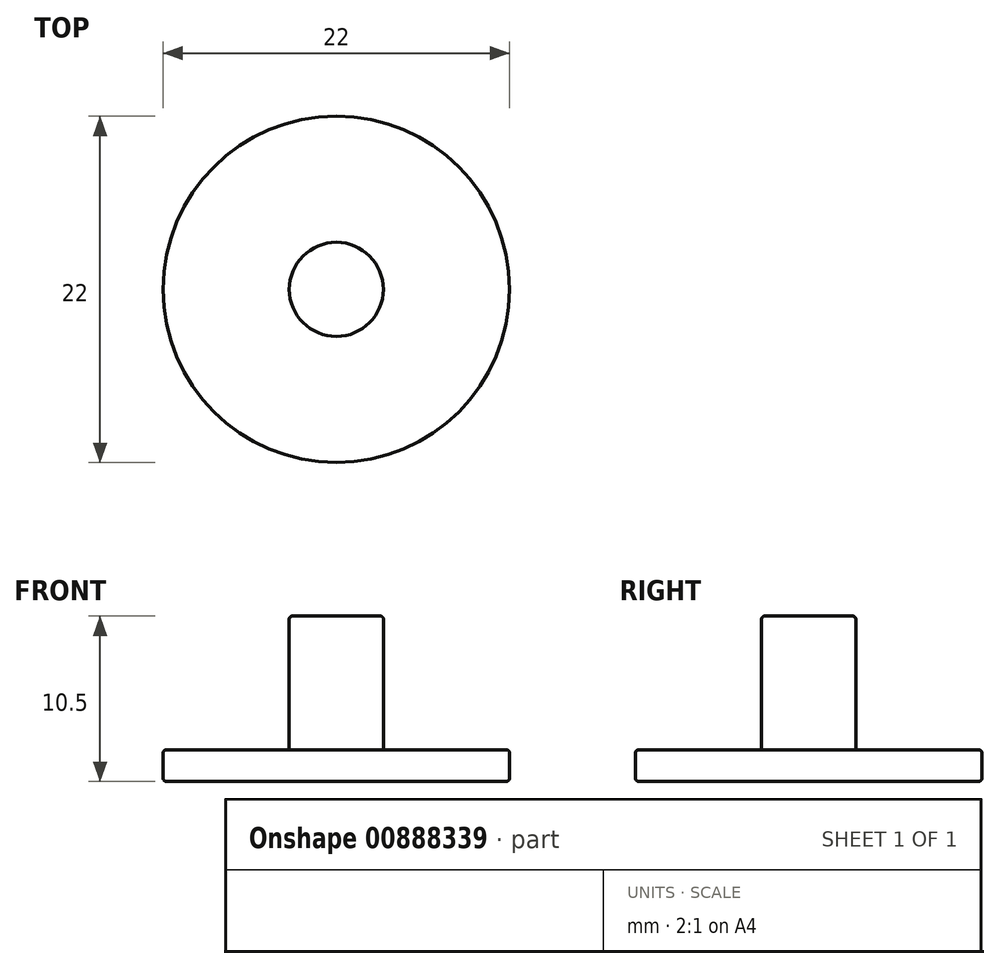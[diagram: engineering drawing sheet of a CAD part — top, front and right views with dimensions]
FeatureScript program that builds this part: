
annotation { "Feature Type Name" : "Feature", "Feature Type Description" : "" }
export const myFeature = defineFeature(function(context is Context, id is Id, definition is map)
    precondition{}
    {
        {
            var Q0;
            Q0=qCreatedBy(makeId("Top.planeOp"),FACE);
            var sketch = newSketch(context, id + "F0", { "sketchPlane" : qUnion([Q0])});
            skCircle(sketch, "E0", {"center": v(0, 0) * mm, "radius": 11 * mm});
            skSolve(sketch);
        }
        {
            var Q0;
            Q0 = qSketchRegion(id + "F0", true);
            extrude(context, id + "F1", {"entities" : qUnion([Q0]), "depth" : 2 * mm, "offsetDistance" : 25.4 * mm});
        }
        {
            var Q0;
            Q0=makeQuery(id+"F1.opExtrude","CAP_FACE",FACE,{"disambiguationData":[OSD([sQuery(id+"F0.wireOp",EDGE,"E0")])],"isStart":false});
            var sketch = newSketch(context, id + "F2", { "sketchPlane" : qUnion([Q0])});
            skCircle(sketch, "E1", {"center": v(0, 0) * mm, "radius": 3 * mm});
            skSolve(sketch);
        }
        {
            var Q0;
            Q0=makeQuery(id+"F2.imprint","IMPRINT",FACE,{"disambiguationData":[TD([[makeQuery(id+"F2.imprint","IMPRINT",EDGE,{"derivedFrom":sQuery(id+"F2.wireOp",EDGE,"E1")}),1.0]])]});
            extrude(context, id + "F3", {"entities" : qUnion([Q0]), "operationType" : NewBodyOperationType.ADD, "depth" : 8.5 * mm, "offsetDistance" : 25.4 * mm});
        }
        {
            var Q0;
            Q0=makeQuery(id+"F1.opExtrude","CAP_EDGE",EDGE,{"disambiguationData":[OSD([sQuery(id+"F0.wireOp",EDGE,"E0")])],"isStart":false});
            var Q1;
            Q1=makeQuery(id+"F1.opExtrude","CAP_EDGE",EDGE,{"disambiguationData":[OSD([sQuery(id+"F0.wireOp",EDGE,"E0")])],"isStart":true});
            var Q2;
            Q2=makeQuery(id+"F3.opExtrude","CAP_EDGE",EDGE,{"disambiguationData":[OSD([sQuery(id+"F2.wireOp",EDGE,"E1")])],"isStart":false});
            fillet(context, id + "F4", {"entities" : qUnion([Q0, Q1, Q2]), "radius" : .2 * mm, "tangentPropagation" : true, "allowEdgeOverflow" : false});
        }
    });
